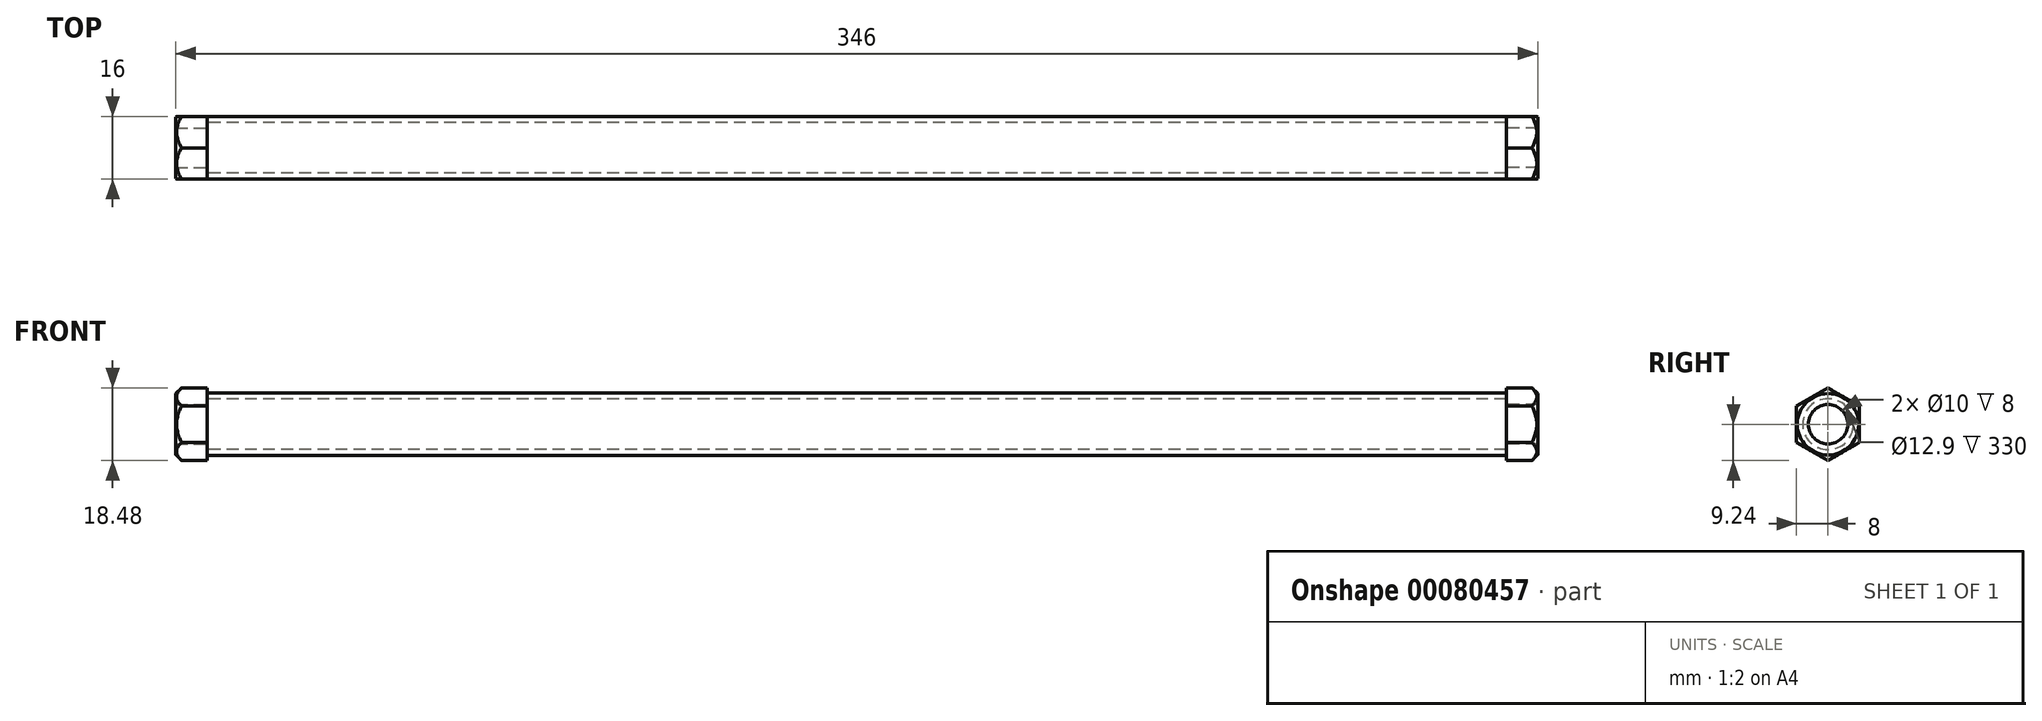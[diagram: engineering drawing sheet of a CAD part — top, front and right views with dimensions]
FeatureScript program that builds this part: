
annotation { "Feature Type Name" : "Feature", "Feature Type Description" : "" }
export const myFeature = defineFeature(function(context is Context, id is Id, definition is map)
    precondition{}
    {
        {
            var Q0;
            Q0=qCreatedBy(makeId("Right.planeOp"),FACE);
            var sketch = newSketch(context, id + "F0", { "sketchPlane" : qUnion([Q0])});
            skCircle(sketch, "E0", {"center": v(0, 0) * mm, "radius": 7.95 * mm});
            skCircle(sketch, "E1", {"center": v(0, 0) * mm, "radius": 6.45 * mm});
            skSolve(sketch);
        }
        {
            var Q0;
            Q0 = qSketchRegion(id + "F0", true);
            extrude(context, id + "F1", {"entities" : qUnion([Q0]), "depth" : 330 * mm, "symmetric" : true});
        }
        {
            var Q0;
            Q0=makeQuery(id+"F1.opExtrude","CAP_FACE",FACE,{"disambiguationData":[OSD([sQuery(id+"F0.wireOp",EDGE,"E0"),sQuery(id+"F0.wireOp",EDGE,"E1")])],"isStart":false});
            var sketch = newSketch(context, id + "F2", { "sketchPlane" : qUnion([Q0])});
            skCircle(sketch, "E2", {"center": v(0, 0) * mm, "radius": 5 * mm});
            skCircle(sketch, "E3.cCircle", {"center": v(0, 0) * mm, "radius": 8 * mm, "construction": true});
            skLineSegment(sketch, "E3.0", {"start": v(8, 4.62) * mm, "end": v(8, -4.62) * mm});
            skLineSegment(sketch, "E3.1", {"start": v(8, -4.62) * mm, "end": v(0, -9.24) * mm});
            skLineSegment(sketch, "E3.2", {"start": v(0, -9.24) * mm, "end": v(-8, -4.62) * mm});
            skLineSegment(sketch, "E3.3", {"start": v(-8, -4.62) * mm, "end": v(-8, 4.62) * mm});
            skLineSegment(sketch, "E3.4", {"start": v(-8, 4.62) * mm, "end": v(0, 9.24) * mm});
            skLineSegment(sketch, "E3.5", {"start": v(0, 9.24) * mm, "end": v(8, 4.62) * mm});
            skPoint(sketch, "E3.0.midPoint", {"position": v(8, 0) * mm});
            skSolve(sketch);
        }
        {
            var Q0;
            Q0 = qSketchRegion(id + "F2", true);
            extrude(context, id + "F3", {"entities" : qUnion([Q0]), "depth" : 8 * mm});
        }
        {
            var Q0;
            Q0=qCreatedBy(makeId("Front.planeOp"),FACE);
            var sketch = newSketch(context, id + "F4", { "sketchPlane" : qUnion([Q0])});
            skPoint(sketch, "E4.0", {"position": v(173, 9.24) * mm});
            skLineSegment(sketch, "E5", {"start": v(173, 9.24) * mm, "end": v(171.55, 9.24) * mm});
            skLineSegment(sketch, "E6", {"start": v(171.55, 9.24) * mm, "end": v(173, 7.79) * mm});
            skLineSegment(sketch, "E7", {"start": v(173, 7.79) * mm, "end": v(173, 9.24) * mm});
            skLineSegment(sketch, "E8", {"start": v(0, 0) * mm, "end": v(232.31, 0) * mm, "construction": true});
            skSolve(sketch);
        }
        {
            var Q0;
            Q0 = qSketchRegion(id + "F4", true);
            var Q1;
            Q1=sQuery(id+"F4.wireOp",EDGE,"E8");
            revolve(context, id + "F5", {"operationType" : NewBodyOperationType.REMOVE, "entities" : qUnion([Q0]), "axis" : qUnion([Q1]), "revolveType" : RevolveType.FULL, "oppositeDirection" : true});
        }
        {
            var Q0;
            Q0=makeQuery(id+"F3.opExtrude","SWEPT_BODY",BODY,{"disambiguationData":[OSD([sQuery(id+"F2.wireOp",EDGE,"E2"),sQuery(id+"F2.wireOp",EDGE,"E3.0"),sQuery(id+"F2.wireOp",EDGE,"E3.1"),sQuery(id+"F2.wireOp",EDGE,"E3.2"),sQuery(id+"F2.wireOp",EDGE,"E3.3"),sQuery(id+"F2.wireOp",EDGE,"E3.4"),sQuery(id+"F2.wireOp",EDGE,"E3.5")])]});
            var Q1;
            Q1=qCreatedBy(makeId("Right.planeOp"),FACE);
            mirror(context, id + "F6", {"entities" : qUnion([Q0]), "mirrorPlane" : qUnion([Q1])});
        }
    });
